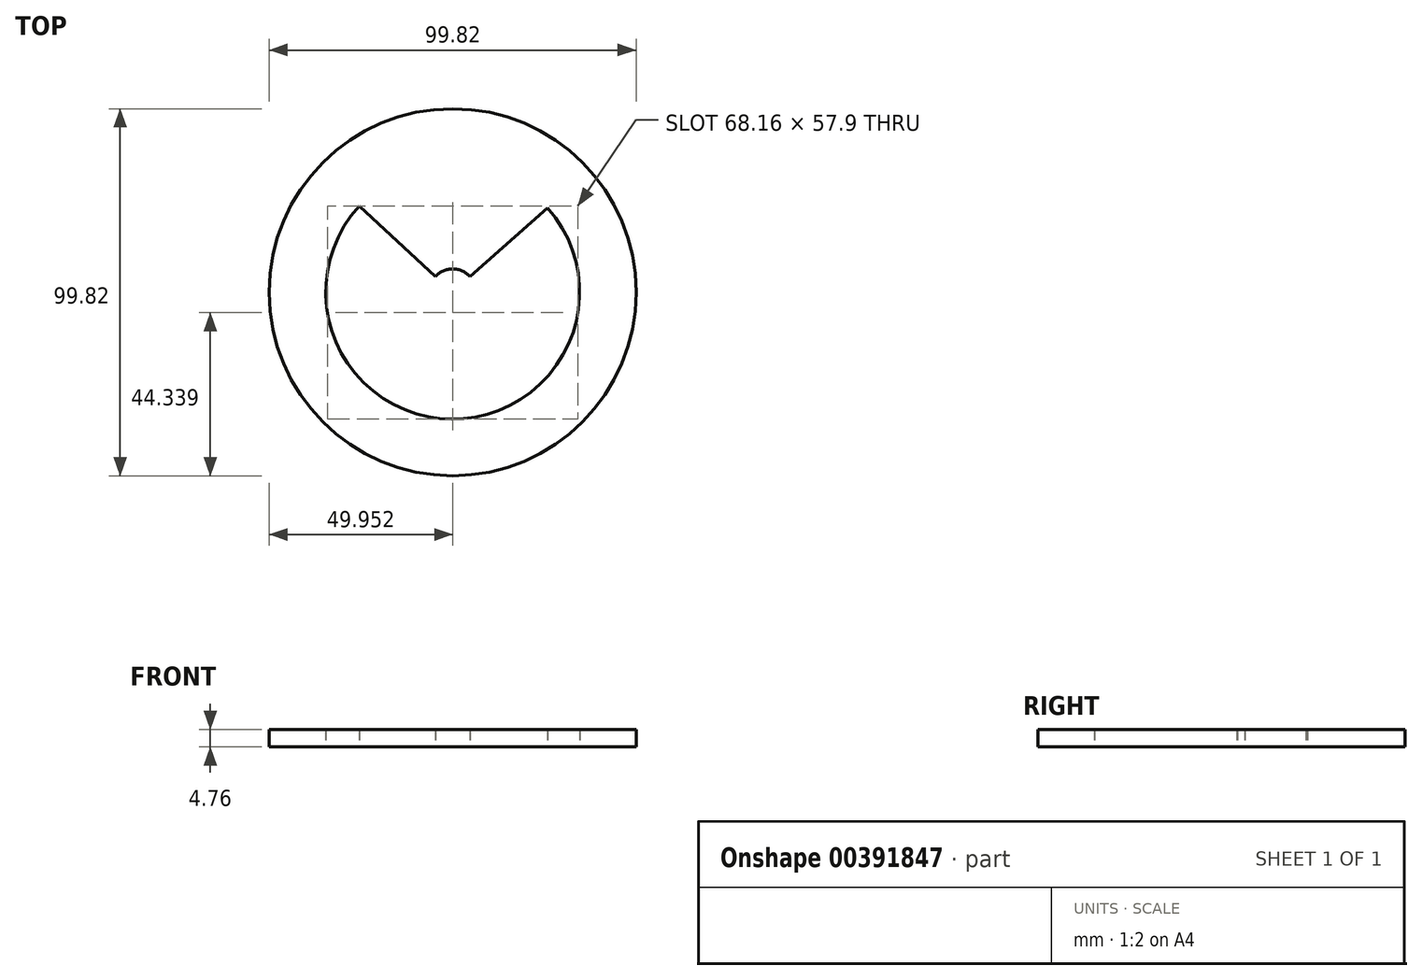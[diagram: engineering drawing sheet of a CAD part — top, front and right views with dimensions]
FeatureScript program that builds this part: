
annotation { "Feature Type Name" : "Feature", "Feature Type Description" : "" }
export const myFeature = defineFeature(function(context is Context, id is Id, definition is map)
    precondition{}
    {
        {
            var Q0;
            Q0=qCreatedBy(makeId("Top.planeOp"),FACE);
            var sketch = newSketch(context, id + "F0", { "sketchPlane" : qUnion([Q0])});
            skCircle(sketch, "E0", {"center": v(0, 0) * mm, "radius": 49.91 * mm});
            skCircle(sketch, "E1", {"center": v(0, 0) * mm, "radius": 6.35 * mm});
            skSolve(sketch);
        }
        {
            var Q0;
            Q0=makeQuery(id+"F0.imprint","IMPRINT",FACE,{"disambiguationData":[TD([[makeQuery(id+"F0.imprint","IMPRINT",EDGE,{"derivedFrom":sQuery(id+"F0.wireOp",EDGE,"E0")}),1.0]])]});
            extrude(context, id + "F1", {"entities" : qUnion([Q0]), "depth" : 4.76 * mm});
        }
        {
            var Q0;
            Q0=makeQuery(id+"F1.opExtrude","CAP_FACE",FACE,{"disambiguationData":[OSD([sQuery(id+"F0.wireOp",EDGE,"E0"),sQuery(id+"F0.wireOp",EDGE,"E1")])],"isStart":true});
            var sketch = newSketch(context, id + "F2", { "sketchPlane" : qUnion([Q0])});
            skCircle(sketch, "E2", {"center": v(0, 0) * mm, "radius": 34.52 * mm});
            skLineSegment(sketch, "E3", {"start": v(0, 0) * mm, "end": v(-25.4, -23.38) * mm});
            skLineSegment(sketch, "E4", {"start": v(0, 0) * mm, "end": v(25.75, -22.99) * mm});
            skSolve(sketch);
        }
        {
            var Q0;
            {var subQ0=sQuery(id+"F2.wireOp",EDGE,"E3");var subQ1=sQuery(id+"F2.wireOp",EDGE,"E2");var subQ2=makeQuery(id+"F2.imprint","INTERSECT",VERTEX,{"derivedFrom":[subQ1,subQ0]});Q0=makeQuery(id+"F2.imprint","IMPRINT",FACE,{"disambiguationData":[TD([[makeQuery(id+"F2.imprint","IMPRINT",EDGE,{"disambiguationData":[TD([[subQ2,1.0]])],"derivedFrom":subQ1}),1.0]])]});}
            extrude(context, id + "F3", {"entities" : qUnion([Q0]), "operationType" : NewBodyOperationType.REMOVE, "oppositeDirection" : true, "depth" : 9.14 * mm});
        }
    });
